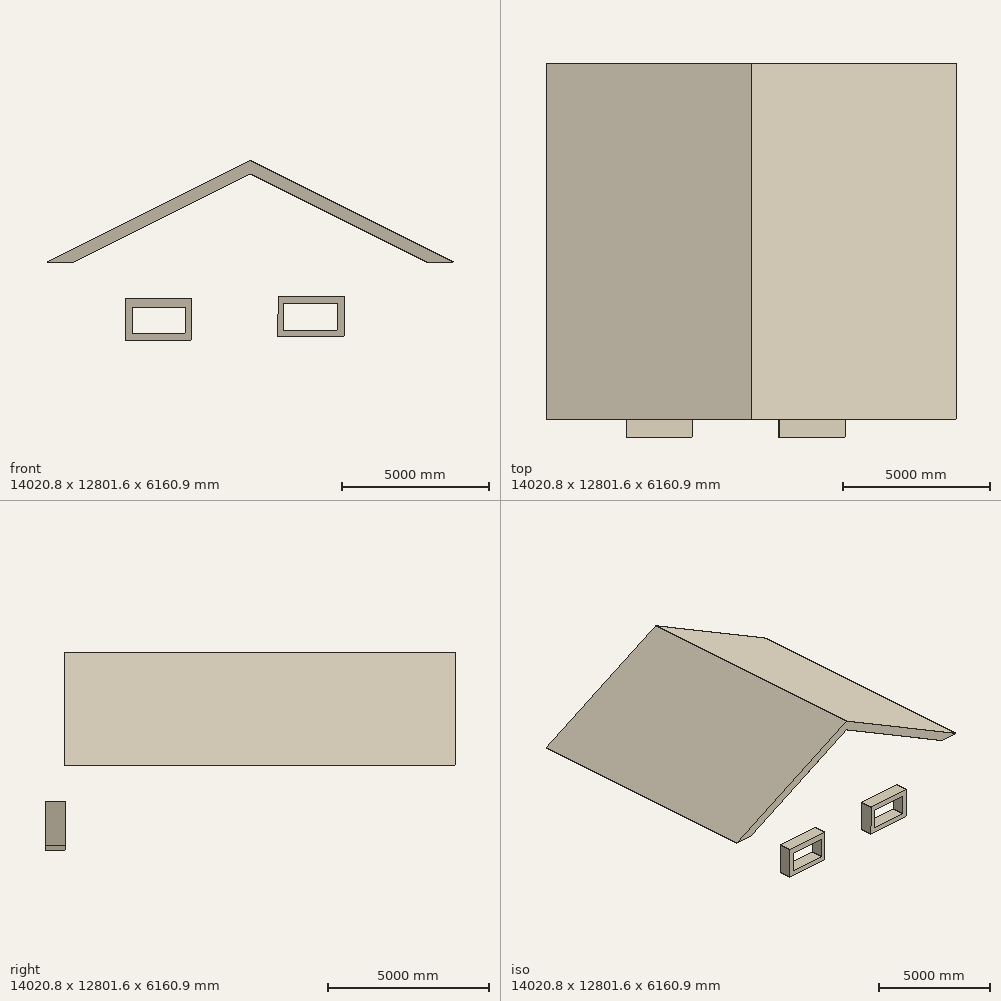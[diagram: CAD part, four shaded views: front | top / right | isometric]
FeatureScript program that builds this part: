
annotation { "Feature Type Name" : "Feature", "Feature Type Description" : "" }
export const myFeature = defineFeature(function(context is Context, id is Id, definition is map)
    precondition{}
    {
        {
            var Q0;
            Q0=qCreatedBy(makeId("Front.planeOp"),FACE);
            var sketch = newSketch(context, id + "F0", { "sketchPlane" : qUnion([Q0])});
            skLineSegment(sketch, "E0", {"start": v(0, 0) * mm, "end": v(-6096, 0) * mm});
            skLineSegment(sketch, "E1", {"start": v(0, 0) * mm, "end": v(6096, 0) * mm});
            skLineSegment(sketch, "E2", {"start": v(0, 0) * mm, "end": v(0, 3048) * mm, "construction": true});
            skLineSegment(sketch, "E3", {"start": v(0, 3048) * mm, "end": v(-6096, 0) * mm});
            skLineSegment(sketch, "E4", {"start": v(0, 3048) * mm, "end": v(6096, 0) * mm});
            skLineSegment(sketch, "E5", {"start": v(-6096, 0) * mm, "end": v(-7010.4, 0) * mm});
            skLineSegment(sketch, "E6", {"start": v(0, 3048) * mm, "end": v(0, 3505.2) * mm});
            skLineSegment(sketch, "E7", {"start": v(-7010.4, 0) * mm, "end": v(0, 3505.2) * mm});
            skLineSegment(sketch, "E8", {"start": v(6096, 0) * mm, "end": v(7010.4, 0) * mm});
            skLineSegment(sketch, "E9", {"start": v(0, 3505.2) * mm, "end": v(7010.4, 0) * mm});
            skLineSegment(sketch, "E10", {"start": v(-6096, 0) * mm, "end": v(-6096, -7315.2) * mm});
            skLineSegment(sketch, "E11", {"start": v(6096, 0) * mm, "end": v(6096, -7315.2) * mm});
            skLineSegment(sketch, "E12", {"start": v(-6096, -7315.2) * mm, "end": v(6096, -7315.2) * mm});
            skLineSegment(sketch, "E13", {"start": v(0, 0) * mm, "end": v(0, -7315.2) * mm, "construction": true});
            skLineSegment(sketch, "E14", {"start": v(0, -7315.2) * mm, "end": v(457.2, -7315.2) * mm});
            skLineSegment(sketch, "E15", {"start": v(0, -7315.2) * mm, "end": v(-457.2, -7315.2) * mm});
            skLineSegment(sketch, "E16", {"start": v(-457.2, -7315.2) * mm, "end": v(-457.2, -5181.6) * mm});
            skLineSegment(sketch, "E17", {"start": v(-457.2, -5181.6) * mm, "end": v(0, -5181.6) * mm});
            skLineSegment(sketch, "E18", {"start": v(0, -5181.6) * mm, "end": v(457.2, -5181.6) * mm});
            skLineSegment(sketch, "E19", {"start": v(457.2, -5181.6) * mm, "end": v(457.2, -7315.2) * mm});
            skLineSegment(sketch, "E20", {"start": v(-6096, -3657.6) * mm, "end": v(6096, -3657.6) * mm, "construction": true});
            skLineSegment(sketch, "E21", {"start": v(-4043.63, -1510) * mm, "end": v(-2214.83, -1510) * mm});
            skLineSegment(sketch, "E22", {"start": v(-4043.63, -1510) * mm, "end": v(-4043.63, -2424.4) * mm});
            skLineSegment(sketch, "E23", {"start": v(-4043.63, -2424.4) * mm, "end": v(-2214.83, -2424.4) * mm});
            skLineSegment(sketch, "E24", {"start": v(-2214.83, -2424.4) * mm, "end": v(-2214.83, -1510) * mm});
            skLineSegment(sketch, "E25", {"start": v(-4257.73, -1221.52) * mm, "end": v(-4257.73, -2655.7) * mm});
            skLineSegment(sketch, "E26", {"start": v(-4257.73, -2655.7) * mm, "end": v(-2016.82, -2655.7) * mm});
            skLineSegment(sketch, "E27", {"start": v(-4257.73, -1221.52) * mm, "end": v(-2016.82, -1221.52) * mm});
            skLineSegment(sketch, "E28", {"start": v(-2016.82, -2655.7) * mm, "end": v(-2016.82, -1221.52) * mm});
            skLineSegment(sketch, "E29", {"start": v(1142.86, -1382.76) * mm, "end": v(1142.86, -2297.16) * mm});
            skLineSegment(sketch, "E30", {"start": v(1142.86, -2297.16) * mm, "end": v(2971.66, -2297.16) * mm});
            skLineSegment(sketch, "E31", {"start": v(2971.66, -2297.16) * mm, "end": v(2971.66, -1382.76) * mm});
            skLineSegment(sketch, "E32", {"start": v(1142.86, -1382.76) * mm, "end": v(2971.66, -1382.76) * mm});
            skLineSegment(sketch, "E33", {"start": v(-6096, -7315.2) * mm, "end": v(-6096, -7693.18) * mm});
            skLineSegment(sketch, "E34", {"start": v(-6096, -7693.18) * mm, "end": v(6006.79, -7693.18) * mm});
            skLineSegment(sketch, "E35", {"start": v(6096, -7315.2) * mm, "end": v(6096, -7693.18) * mm});
            skLineSegment(sketch, "E36", {"start": v(950.87, -1131.52) * mm, "end": v(3223.67, -1131.52) * mm});
            skLineSegment(sketch, "E37", {"start": v(3223.67, -1131.52) * mm, "end": v(3223.67, -2523.04) * mm});
            skLineSegment(sketch, "E38", {"start": v(3246.87, -2523.04) * mm, "end": v(927.68, -2523.04) * mm});
            skLineSegment(sketch, "E39", {"start": v(927.68, -2523.04) * mm, "end": v(950.87, -1131.52) * mm});
            skSolve(sketch);
        }
        {
            var Q0;
            Q0=makeQuery(id+"F0.imprint","IMPRINT",FACE,{"disambiguationData":[TD([[makeQuery(id+"F0.imprint","IMPRINT",EDGE,{"derivedFrom":sQuery(id+"F0.wireOp",EDGE,"E3")}),-1.0]])]});
            var Q1;
            Q1=makeQuery(id+"F0.imprint","IMPRINT",FACE,{"disambiguationData":[TD([[makeQuery(id+"F0.imprint","IMPRINT",EDGE,{"derivedFrom":sQuery(id+"F0.wireOp",EDGE,"E4")}),1.0]])]});
            extrude(context, id + "F1", {"entities" : qUnion([Q0, Q1]), "depth" : -12192 * mm, "offsetDistance" : 30.48 * mm});
        }
        {
            var Q0;
            Q0=makeQuery(id+"F0.imprint","IMPRINT",FACE,{"disambiguationData":[TD([[makeQuery(id+"F0.imprint","IMPRINT",EDGE,{"derivedFrom":sQuery(id+"F0.wireOp",EDGE,"E21")}),1.0]])]});
            extrude(context, id + "F2", {"entities" : qUnion([Q0]), "depth" : 609.6 * mm, "offsetDistance" : 30.48 * mm});
        }
        {
            var Q0;
            Q0=makeQuery(id+"F0.imprint","IMPRINT",FACE,{"disambiguationData":[TD([[makeQuery(id+"F0.imprint","IMPRINT",EDGE,{"derivedFrom":sQuery(id+"F0.wireOp",EDGE,"E29")}),-1.0]])]});
            extrude(context, id + "F3", {"entities" : qUnion([Q0]), "depth" : 609.6 * mm, "offsetDistance" : 30.48 * mm});
        }
    });
